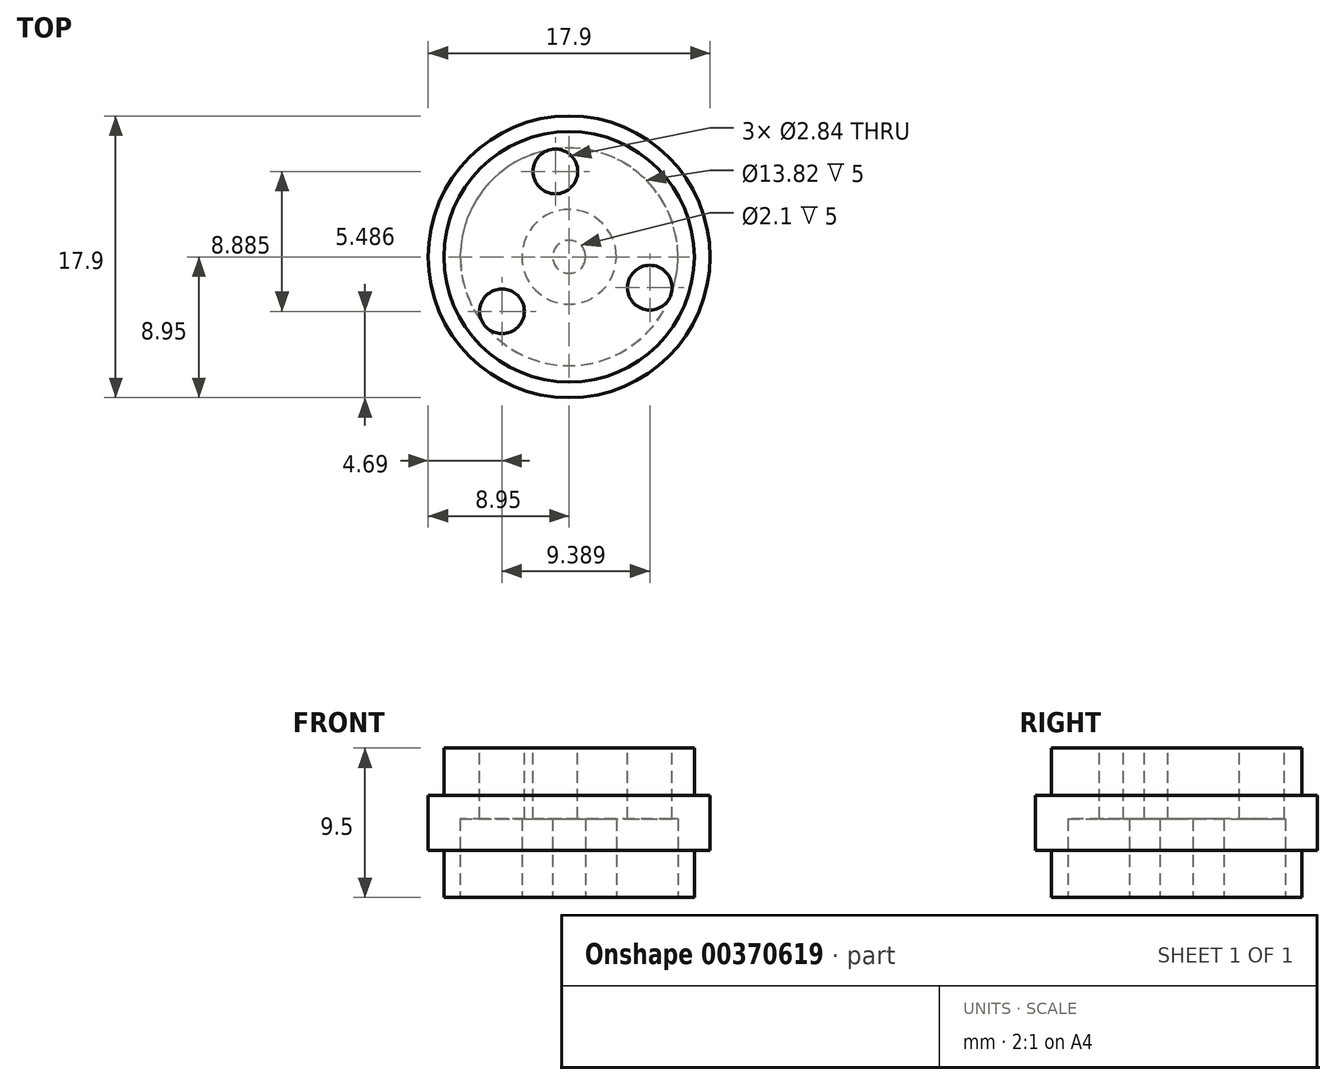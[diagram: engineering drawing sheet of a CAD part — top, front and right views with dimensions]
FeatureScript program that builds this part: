
annotation { "Feature Type Name" : "Feature", "Feature Type Description" : "" }
export const myFeature = defineFeature(function(context is Context, id is Id, definition is map)
    precondition{}
    {
        {
            var Q0;
            Q0=qCreatedBy(makeId("Top.planeOp"),FACE);
            var sketch = newSketch(context, id + "F0", { "sketchPlane" : qUnion([Q0])});
            skCircle(sketch, "E0", {"center": v(0, 0) * mm, "radius": 7.95 * mm});
            skSolve(sketch);
        }
        {
            var Q0;
            Q0 = qSketchRegion(id + "F0", true);
            extrude(context, id + "F1", {"entities" : qUnion([Q0]), "depth" : 3 * mm});
        }
        {
            var Q0;
            Q0=makeQuery(id+"F1.opExtrude","CAP_FACE",FACE,{"disambiguationData":[OSD([sQuery(id+"F0.wireOp",EDGE,"E0")])],"isStart":false});
            var sketch = newSketch(context, id + "F2", { "sketchPlane" : qUnion([Q0])});
            skCircle(sketch, "E1", {"center": v(0, 0) * mm, "radius": 8.95 * mm});
            skSolve(sketch);
        }
        {
            var Q0;
            Q0 = qSketchRegion(id + "F2", true);
            extrude(context, id + "F3", {"entities" : qUnion([Q0]), "operationType" : NewBodyOperationType.ADD, "depth" : 3.5 * mm});
        }
        {
            var Q0;
            Q0=makeQuery(id+"F3.opExtrude","CAP_FACE",FACE,{"disambiguationData":[OSD([sQuery(id+"F2.wireOp",EDGE,"E1")])],"isStart":false});
            var sketch = newSketch(context, id + "F4", { "sketchPlane" : qUnion([Q0])});
            skCircle(sketch, "E2", {"center": v(0, 0) * mm, "radius": 7.95 * mm});
            skSolve(sketch);
        }
        {
            var Q0;
            Q0 = qSketchRegion(id + "F4", true);
            extrude(context, id + "F5", {"entities" : qUnion([Q0]), "operationType" : NewBodyOperationType.ADD, "depth" : 3 * mm});
        }
        {
            var Q0;
            Q0=makeQuery(id+"F5.opExtrude","CAP_FACE",FACE,{"disambiguationData":[OSD([sQuery(id+"F4.wireOp",EDGE,"E2")])],"isStart":false});
            var sketch = newSketch(context, id + "F6", { "sketchPlane" : qUnion([Q0])});
            skCircle(sketch, "E3", {"center": v(0, 0) * mm, "radius": 5.5 * mm, "construction": true});
            skCircle(sketch, "E4", {"center": v(-0.87, 5.42) * mm, "radius": 1.42 * mm});
            skCircle(sketch, "E5.1.0", {"center": v(-4.26, -3.46) * mm, "radius": 1.42 * mm});
            skCircle(sketch, "E5.2.0", {"center": v(5.13, -1.96) * mm, "radius": 1.42 * mm});
            skSolve(sketch);
        }
        {
            var Q0;
            Q0 = qSketchRegion(id + "F6", true);
            extrude(context, id + "F7", {"entities" : qUnion([Q0]), "operationType" : NewBodyOperationType.REMOVE, "endBound" : BoundingType.THROUGH_ALL, "oppositeDirection" : true, "depth" : 25 * mm});
        }
        {
            var Q0;
            Q0=makeQuery(id+"F1.opExtrude","CAP_FACE",FACE,{"disambiguationData":[OSD([sQuery(id+"F0.wireOp",EDGE,"E0")])],"isStart":true});
            var sketch = newSketch(context, id + "F8", { "sketchPlane" : qUnion([Q0])});
            skCircle(sketch, "E6", {"center": v(0, 0) * mm, "radius": 1.05 * mm});
            skCircle(sketch, "E7", {"center": v(0, 0) * mm, "radius": 3 * mm});
            skCircle(sketch, "E8", {"center": v(0, 0) * mm, "radius": 6.91 * mm});
            skSolve(sketch);
        }
        {
            var Q0;
            Q0 = qSketchRegion(id + "F8", true);
            var Q1;
            Q1=makeQuery(id+"F8.imprint","IMPRINT",FACE,{"disambiguationData":[TD([[makeQuery(id+"F8.imprint","IMPRINT",EDGE,{"derivedFrom":sQuery(id+"F8.wireOp",EDGE,"E6")}),1.0]])]});
            extrude(context, id + "F9", {"entities" : qUnion([Q0, Q1]), "operationType" : NewBodyOperationType.REMOVE, "oppositeDirection" : true, "depth" : 5 * mm});
        }
    });
